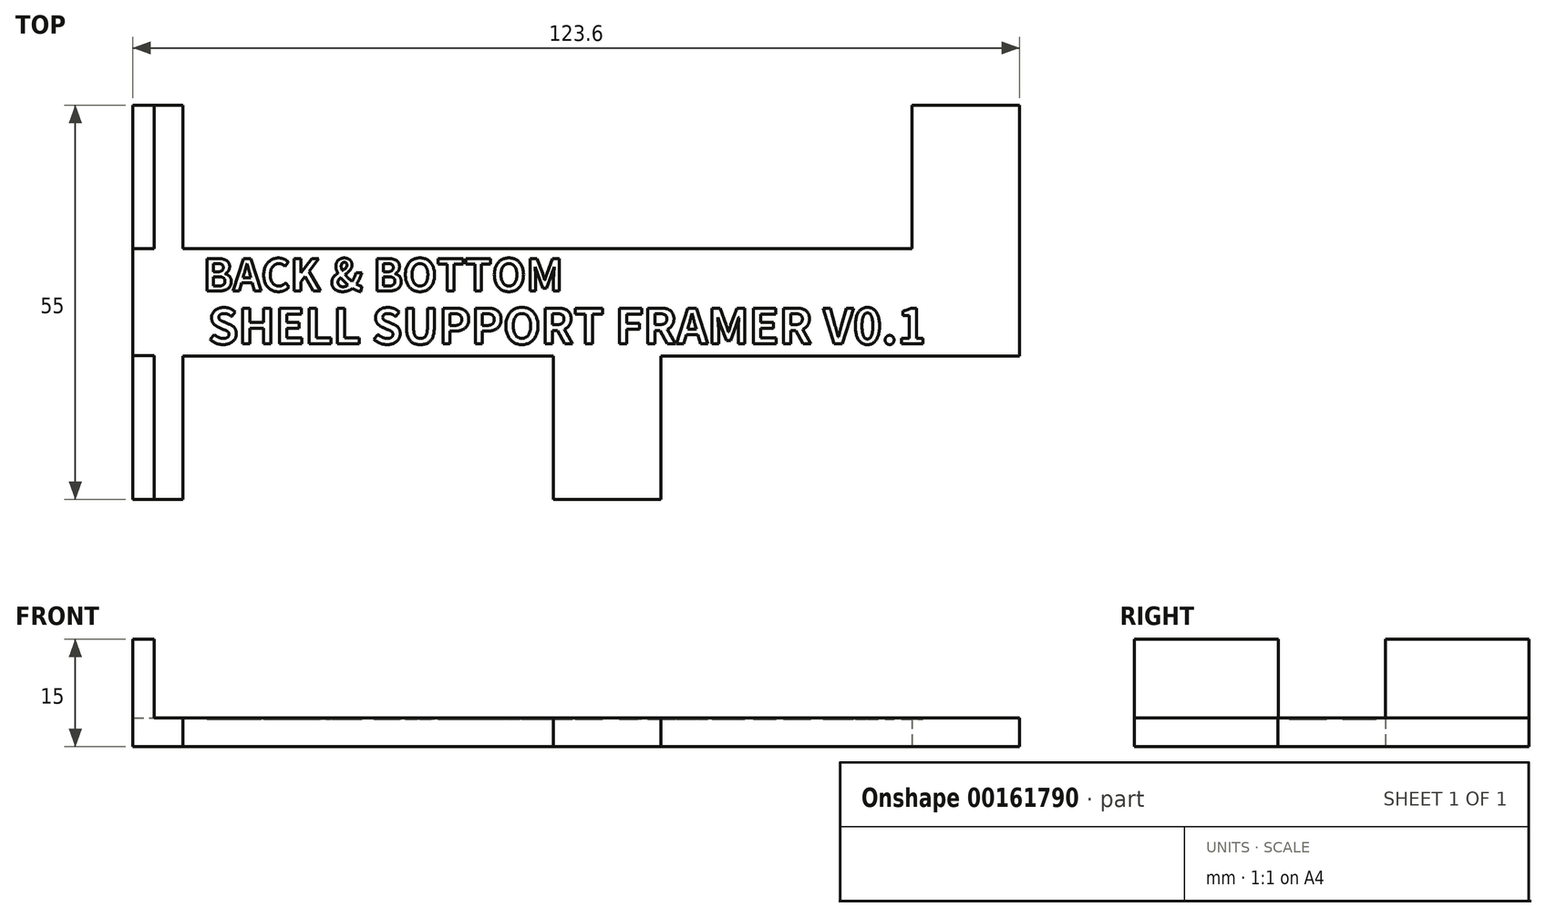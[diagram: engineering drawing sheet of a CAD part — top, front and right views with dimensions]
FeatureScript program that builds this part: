
annotation { "Feature Type Name" : "Feature", "Feature Type Description" : "" }
export const myFeature = defineFeature(function(context is Context, id is Id, definition is map)
    precondition{}
    {
        {
            var Q0;
            Q0=qCreatedBy(makeId("Top.planeOp"),FACE);
            var sketch = newSketch(context, id + "F0", { "sketchPlane" : qUnion([Q0])});
            skLineSegment(sketch, "E0.bottom", {"start": v(-46.59, 22.7) * mm, "end": v(-11.59, 22.7) * mm});
            skLineSegment(sketch, "E0.top", {"start": v(-46.59, 7.7) * mm, "end": v(-26.59, 7.7) * mm});
            skLineSegment(sketch, "E0.left", {"start": v(-46.59, 22.7) * mm, "end": v(-46.59, 7.7) * mm});
            skLineSegment(sketch, "E0.right", {"start": v(-11.59, 22.7) * mm, "end": v(-11.59, 7.7) * mm});
            skLineSegment(sketch, "E1.bottom", {"start": v(-11.59, 22.7) * mm, "end": v(-26.59, 22.7) * mm});
            skLineSegment(sketch, "E1.top", {"start": v(-11.59, -100.9) * mm, "end": v(-26.59, -100.9) * mm});
            skLineSegment(sketch, "E1.left", {"start": v(-11.59, 22.7) * mm, "end": v(-11.59, -27.3) * mm});
            skLineSegment(sketch, "E1.right", {"start": v(-26.59, 7.7) * mm, "end": v(-26.59, -93.9) * mm});
            skLineSegment(sketch, "E2.bottom", {"start": v(-46.59, -100.9) * mm, "end": v(-26.59, -100.9) * mm});
            skLineSegment(sketch, "E2.top", {"start": v(-46.59, -93.9) * mm, "end": v(-26.59, -93.9) * mm});
            skLineSegment(sketch, "E2.left", {"start": v(-46.59, -100.9) * mm, "end": v(-46.59, -93.9) * mm});
            skLineSegment(sketch, "E3.bottom", {"start": v(-11.59, -100.9) * mm, "end": v(8.41, -100.9) * mm});
            skLineSegment(sketch, "E3.top", {"start": v(-11.59, -93.9) * mm, "end": v(8.41, -93.9) * mm});
            skLineSegment(sketch, "E3.right", {"start": v(8.41, -100.9) * mm, "end": v(8.41, -93.9) * mm});
            skLineSegment(sketch, "E4", {"start": v(-11.59, -100.9) * mm, "end": v(-11.59, -42.3) * mm, "construction": true});
            skLineSegment(sketch, "E5", {"start": v(-11.59, -42.3) * mm, "end": v(8.41, -42.3) * mm});
            skLineSegment(sketch, "E6", {"start": v(8.41, -42.3) * mm, "end": v(8.41, -27.3) * mm});
            skLineSegment(sketch, "E7", {"start": v(8.41, -27.3) * mm, "end": v(-11.59, -27.3) * mm});
            skLineSegment(sketch, "E8.trimOffspring", {"start": v(-11.59, -42.3) * mm, "end": v(-11.59, -93.9) * mm});
            skSolve(sketch);
        }
        {
            var Q0;
            Q0 = qSketchRegion(id + "F0", true);
            extrude(context, id + "F1", {"entities" : qUnion([Q0]), "depth" : 4 * mm});
        }
        {
            var Q0;
            Q0=makeQuery(id+"F1.opExtrude","CAP_FACE",FACE,{"disambiguationData":[OSD([sQuery(id+"F0.wireOp",EDGE,"E0.bottom"),sQuery(id+"F0.wireOp",EDGE,"E0.top"),sQuery(id+"F0.wireOp",EDGE,"E0.left"),sQuery(id+"F0.wireOp",EDGE,"E1.bottom"),sQuery(id+"F0.wireOp",EDGE,"E1.top"),sQuery(id+"F0.wireOp",EDGE,"E1.left"),sQuery(id+"F0.wireOp",EDGE,"E1.right"),sQuery(id+"F0.wireOp",EDGE,"E2.bottom"),sQuery(id+"F0.wireOp",EDGE,"E2.top"),sQuery(id+"F0.wireOp",EDGE,"E2.left"),sQuery(id+"F0.wireOp",EDGE,"E3.bottom"),sQuery(id+"F0.wireOp",EDGE,"E3.top"),sQuery(id+"F0.wireOp",EDGE,"E3.right"),sQuery(id+"F0.wireOp",EDGE,"E5"),sQuery(id+"F0.wireOp",EDGE,"E6"),sQuery(id+"F0.wireOp",EDGE,"E7"),sQuery(id+"F0.wireOp",EDGE,"E8.trimOffspring")])],"isStart":false});
            var sketch = newSketch(context, id + "F2", { "sketchPlane" : qUnion([Q0])});
            skLineSegment(sketch, "E9.bottom", {"start": v(-46.59, -100.9) * mm, "end": v(-26.59, -100.9) * mm});
            skLineSegment(sketch, "E9.top", {"start": v(-46.59, -97.9) * mm, "end": v(-26.59, -97.9) * mm});
            skLineSegment(sketch, "E9.left", {"start": v(-46.59, -100.9) * mm, "end": v(-46.59, -97.9) * mm});
            skLineSegment(sketch, "E9.right", {"start": v(-26.59, -100.9) * mm, "end": v(-26.59, -97.9) * mm});
            skLineSegment(sketch, "E10.bottom", {"start": v(8.41, -100.9) * mm, "end": v(-11.66, -100.9) * mm});
            skLineSegment(sketch, "E10.top", {"start": v(8.41, -97.9) * mm, "end": v(-11.66, -97.9) * mm});
            skLineSegment(sketch, "E10.left", {"start": v(8.41, -100.9) * mm, "end": v(8.41, -97.9) * mm});
            skLineSegment(sketch, "E10.right", {"start": v(-11.66, -100.9) * mm, "end": v(-11.66, -97.9) * mm});
            skSolve(sketch);
        }
        {
            var Q0;
            Q0 = qSketchRegion(id + "F2", true);
            extrude(context, id + "F3", {"entities" : qUnion([Q0]), "operationType" : NewBodyOperationType.ADD, "depth" : 11 * mm});
        }
        {
            var Q0;
            Q0=makeQuery(id+"F1.opExtrude","SWEPT_BODY",BODY,{"disambiguationData":[OSD([sQuery(id+"F0.wireOp",EDGE,"E0.bottom"),sQuery(id+"F0.wireOp",EDGE,"E0.top"),sQuery(id+"F0.wireOp",EDGE,"E0.left"),sQuery(id+"F0.wireOp",EDGE,"E1.bottom"),sQuery(id+"F0.wireOp",EDGE,"E1.top"),sQuery(id+"F0.wireOp",EDGE,"E1.left"),sQuery(id+"F0.wireOp",EDGE,"E1.right"),sQuery(id+"F0.wireOp",EDGE,"E2.bottom"),sQuery(id+"F0.wireOp",EDGE,"E2.top"),sQuery(id+"F0.wireOp",EDGE,"E2.left"),sQuery(id+"F0.wireOp",EDGE,"E3.bottom"),sQuery(id+"F0.wireOp",EDGE,"E3.top"),sQuery(id+"F0.wireOp",EDGE,"E3.right"),sQuery(id+"F0.wireOp",EDGE,"E5"),sQuery(id+"F0.wireOp",EDGE,"E6"),sQuery(id+"F0.wireOp",EDGE,"E7"),sQuery(id+"F0.wireOp",EDGE,"E8.trimOffspring")])]});
            var Q1;
            Q1=makeQuery(id+"F1.opExtrude","SWEPT_EDGE",EDGE,{"disambiguationData":[OSD([sQuery(id+"F0.wireOp",EDGE,"E1.left"),sQuery(id+"F0.wireOp",EDGE,"E7")])]});
            transform(context, id + "F4", {"entities" : qUnion([Q0]), "transformType" : TransformType.ROTATION, "transformAxis" : qUnion([Q1]), "angle" : 90 * degree, "makeCopy" : false});
        }
        {
            var Q0;
            Q0=makeQuery(id+"F1.opExtrude","CAP_FACE",FACE,{"disambiguationData":[OSD([sQuery(id+"F0.wireOp",EDGE,"E0.bottom"),sQuery(id+"F0.wireOp",EDGE,"E0.top"),sQuery(id+"F0.wireOp",EDGE,"E0.left"),sQuery(id+"F0.wireOp",EDGE,"E1.bottom"),sQuery(id+"F0.wireOp",EDGE,"E1.top"),sQuery(id+"F0.wireOp",EDGE,"E1.left"),sQuery(id+"F0.wireOp",EDGE,"E1.right"),sQuery(id+"F0.wireOp",EDGE,"E2.bottom"),sQuery(id+"F0.wireOp",EDGE,"E2.top"),sQuery(id+"F0.wireOp",EDGE,"E2.left"),sQuery(id+"F0.wireOp",EDGE,"E3.bottom"),sQuery(id+"F0.wireOp",EDGE,"E3.top"),sQuery(id+"F0.wireOp",EDGE,"E3.right"),sQuery(id+"F0.wireOp",EDGE,"E5"),sQuery(id+"F0.wireOp",EDGE,"E6"),sQuery(id+"F0.wireOp",EDGE,"E7"),sQuery(id+"F0.wireOp",EDGE,"E8.trimOffspring")])],"isStart":false});
            var sketch = newSketch(context, id + "F5", { "sketchPlane" : qUnion([Q0])});
            skText(sketch, "E11", { "text": "BACK & BOTTOM\n", "fontName": "NotoSansCJKsc-Bold.otf"});
            skPoint(sketch, "E11.firstSnap0", {"position": v(-82.19, -2.3) * mm});
            skPoint(sketch, "E12", {"position": v(-83.69, -27.22) * mm});
            const initialGuessF5  = {"E11": [-0.07539, -0.01823, 1, 0, 0.00442]};
            skSetInitialGuess(sketch, initialGuessF5);
            skSolve(sketch);
        }
        {
            var Q0;
            Q0 = qSketchRegion(id + "F5", true);
            var Q1;
            Q1 = qConstructionFilter(qBodyType(qCreatedBy(id + "F5" ,EDGE), BodyType.WIRE), ConstructionObject.NO);
            extrude(context, id + "F6", {"entities" : qUnion([Q0]), "operationType" : NewBodyOperationType.REMOVE, "surfaceEntities" : qUnion([Q1]), "oppositeDirection" : true, "depth" : .2 * mm});
        }
        {
            var Q0;
            {var subQ0=sQuery(id+"F0.wireOp",EDGE,"E1.left");var subQ1=sQuery(id+"F0.wireOp",EDGE,"E0.left");var subQ2=sQuery(id+"F0.wireOp",EDGE,"E1.right");var subQ3=sQuery(id+"F0.wireOp",EDGE,"E8.trimOffspring");var subQ4=sQuery(id+"F0.wireOp",EDGE,"E5");var subQ5=sQuery(id+"F0.wireOp",EDGE,"E0.top");var subQ6=sQuery(id+"F0.wireOp",EDGE,"E3.bottom");var subQ7=sQuery(id+"F0.wireOp",EDGE,"E2.bottom");var subQ8=sQuery(id+"F0.wireOp",EDGE,"E1.top");var subQ9=sQuery(id+"F0.wireOp",EDGE,"E3.top");var subQ10=sQuery(id+"F0.wireOp",EDGE,"E7");var subQ11=sQuery(id+"F0.wireOp",EDGE,"E6");var subQ12=sQuery(id+"F0.wireOp",EDGE,"E1.bottom");var subQ13=sQuery(id+"F0.wireOp",EDGE,"E0.bottom");var subQ14=sQuery(id+"F0.wireOp",EDGE,"E2.top");var subQ15=sQuery(id+"F0.wireOp",EDGE,"E2.left");var subQ16=sQuery(id+"F0.wireOp",EDGE,"E3.right");Q0=makeQuery(id+"F6.boolean.opBoolean","SPLIT",FACE,{"disambiguationData":[TD([makeQuery(id+"F1.opExtrude","SWEPT_FACE",FACE,{"disambiguationData":[OSD([subQ5])]})])],"derivedFrom":makeQuery(id+"F1.opExtrude","CAP_FACE",FACE,{"disambiguationData":[OSD([subQ13,subQ5,subQ1,subQ12,subQ8,subQ0,subQ2,subQ7,subQ14,subQ15,subQ6,subQ9,subQ16,subQ4,subQ11,subQ10,subQ3])],"isStart":false})});}
            var sketch = newSketch(context, id + "F7", { "sketchPlane" : qUnion([Q0])});
            skText(sketch, "E13", { "text": "SHELL SUPPORT FRAMER V0.1", "fontName": "NotoSansCJKsc-Bold.otf"});
            const initialGuessF7  = {"E13": [-0.0747, -0.0256, 1, 0, 0.00487]};
            skSetInitialGuess(sketch, initialGuessF7);
            skSolve(sketch);
        }
        {
            var Q0;
            Q0 = qSketchRegion(id + "F7", true);
            extrude(context, id + "F8", {"entities" : qUnion([Q0]), "operationType" : NewBodyOperationType.REMOVE, "oppositeDirection" : true, "depth" : .2 * mm});
        }
    });
